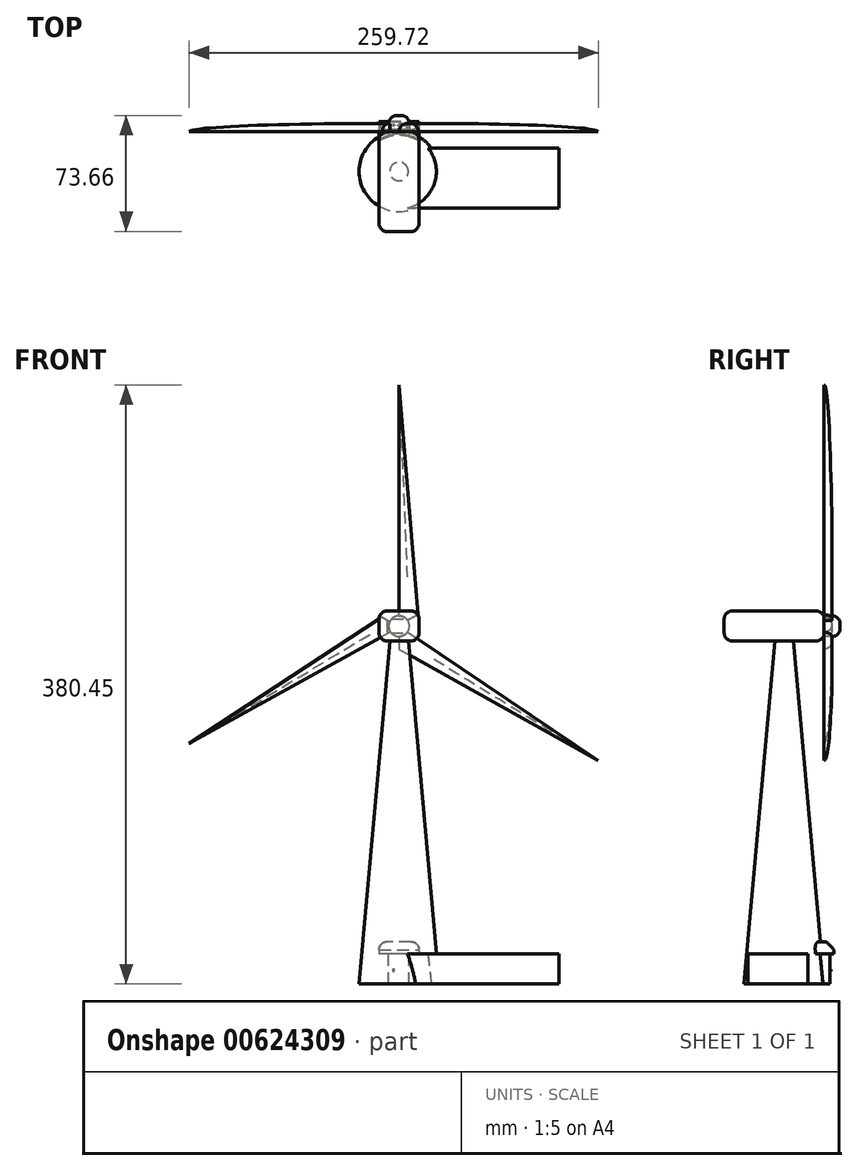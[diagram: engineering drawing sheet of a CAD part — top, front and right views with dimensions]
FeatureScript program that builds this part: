
annotation { "Feature Type Name" : "Feature", "Feature Type Description" : "" }
export const myFeature = defineFeature(function(context is Context, id is Id, definition is map)
    precondition{}
    {
        {
            var Q0;
            Q0=qCreatedBy(makeId("Front.planeOp"),FACE);
            var sketch = newSketch(context, id + "F0", { "sketchPlane" : qUnion([Q0])});
            skLineSegment(sketch, "E0", {"start": v(0, 0) * mm, "end": v(25.4, 0) * mm});
            skLineSegment(sketch, "E1", {"start": v(25.4, 0) * mm, "end": v(5.85, 218.4) * mm});
            skLineSegment(sketch, "E2", {"start": v(5.85, 218.4) * mm, "end": v(0, 217.88) * mm});
            skLineSegment(sketch, "E3", {"start": v(0, 217.88) * mm, "end": v(0, 0) * mm});
            skSolve(sketch);
        }
        {
            var Q0;
            Q0=makeQuery(id+"F0.imprint","IMPRINT",FACE,{"disambiguationData":[TD([[makeQuery(id+"F0.imprint","IMPRINT",EDGE,{"derivedFrom":sQuery(id+"F0.wireOp",EDGE,"E0")}),1.0]])]});
            var Q1;
            Q1=sQuery(id+"F0.wireOp",EDGE,"E3");
            revolve(context, id + "F1", {"entities" : qUnion([Q0]), "axis" : qUnion([Q1]), "revolveType" : RevolveType.FULL});
        }
        {
            var Q0;
            Q0=qCreatedBy(makeId("Top.planeOp"),FACE);
            var Q1;
            Q1 = qBodyType(qCreatedBy(id + "F6bmU4iKGu6LFPM_1" ,EDGE), BodyType.WIRE);
            cPlane(context, id + "F2", {"entities" : qUnion([Q0, Q1]), "cplaneType" : CPlaneType.OFFSET, "offset" : 217.88 * mm, "width" : 152.4 * mm, "height" : 152.4 * mm});
        }
        {
            var Q0;
            Q0=qCreatedBy(id+"F2.planeOp",FACE);
            var sketch = newSketch(context, id + "F3", { "sketchPlane" : qUnion([Q0])});
            skLineSegment(sketch, "E4", {"start": v(0, 0) * mm, "end": v(0, -38.1) * mm});
            skLineSegment(sketch, "E5", {"start": v(0, -38.1) * mm, "end": v(-12.7, -38.1) * mm});
            skLineSegment(sketch, "E6.bottom", {"start": v(-12.7, -38.1) * mm, "end": v(12.7, -38.1) * mm});
            skLineSegment(sketch, "E6.top", {"start": v(-12.7, 25.4) * mm, "end": v(12.7, 25.4) * mm});
            skLineSegment(sketch, "E6.left", {"start": v(-12.7, -38.1) * mm, "end": v(-12.7, 25.4) * mm});
            skLineSegment(sketch, "E6.right", {"start": v(12.7, -38.1) * mm, "end": v(12.7, 25.4) * mm});
            skSolve(sketch);
        }
        {
            var Q0;
            Q0=makeQuery(id+"F3.imprint","IMPRINT",FACE,{"disambiguationData":[TD([[makeQuery(id+"F3.imprint","IMPRINT",EDGE,{"derivedFrom":sQuery(id+"F3.wireOp",EDGE,"E6.top")}),-1.0]])]});
            extrude(context, id + "F4", {"entities" : qUnion([Q0]), "operationType" : NewBodyOperationType.ADD, "depth" : 19.05 * mm, "offsetDistance" : 25.4 * mm});
        }
        {
            var Q0;
            Q0=makeQuery(id+"F4.opExtrude","SWEPT_FACE",FACE,{"disambiguationData":[OSD([sQuery(id+"F3.wireOp",EDGE,"E6.top")])]});
            cPlane(context, id + "F5", {"entities" : qUnion([Q0]), "cplaneType" : CPlaneType.OFFSET, "offset" : 0 * mm, "width" : 152.4 * mm, "height" : 152.4 * mm});
        }
        {
            var Q0;
            Q0=makeQuery(id+"F4.opExtrude","CAP_EDGE",EDGE,{"disambiguationData":[OSD([sQuery(id+"F3.wireOp",EDGE,"E6.left")])],"isStart":false});
            var Q1;
            Q1=makeQuery(id+"F4.opExtrude","CAP_EDGE",EDGE,{"disambiguationData":[OSD([sQuery(id+"F3.wireOp",EDGE,"E6.bottom")])],"isStart":false});
            var Q2;
            Q2=makeQuery(id+"F4.opExtrude","SWEPT_FACE",FACE,{"disambiguationData":[OSD([sQuery(id+"F3.wireOp",EDGE,"E6.bottom")])]});
            var Q3;
            Q3=makeQuery(id+"F4.opExtrude","CAP_EDGE",EDGE,{"disambiguationData":[OSD([sQuery(id+"F3.wireOp",EDGE,"E6.top")])],"isStart":false});
            var Q4;
            Q4=makeQuery(id+"F4.opExtrude","SWEPT_FACE",FACE,{"disambiguationData":[OSD([sQuery(id+"F3.wireOp",EDGE,"E6.top")])]});
            var Q5;
            Q5=makeQuery(id+"F4.opExtrude","CAP_EDGE",EDGE,{"disambiguationData":[OSD([sQuery(id+"F3.wireOp",EDGE,"E6.left")])],"isStart":true});
            var Q6;
            Q6=makeQuery(id+"F4.opExtrude","CAP_EDGE",EDGE,{"disambiguationData":[OSD([sQuery(id+"F3.wireOp",EDGE,"E6.right")])],"isStart":false});
            var Q7;
            Q7=makeQuery(id+"F4.opExtrude","CAP_EDGE",EDGE,{"disambiguationData":[OSD([sQuery(id+"F3.wireOp",EDGE,"E6.right")])],"isStart":true});
            var Q8;
            Q8=makeQuery(id+"F4.opExtrude","SWEPT_FACE",FACE,{"disambiguationData":[OSD([sQuery(id+"F3.wireOp",EDGE,"E6.right")])]});
            fillet(context, id + "F6", {"entities" : qUnion([Q0, Q1, Q2, Q3, Q4, Q5, Q6, Q7, Q8]), "radius" : 5.08 * mm, "tangentPropagation" : true, "allowEdgeOverflow" : false});
        }
        {
            var Q0;
            Q0=qCreatedBy(makeId("Front.planeOp"),FACE);
            var sketch = newSketch(context, id + "F7", { "sketchPlane" : qUnion([Q0])});
            skLineSegment(sketch, "E7.bottom", {"start": v(6.17, 0) * mm, "end": v(-6.53, 0) * mm});
            skLineSegment(sketch, "E7.top", {"start": v(6.17, 19.05) * mm, "end": v(-6.53, 19.05) * mm});
            skLineSegment(sketch, "E7.left", {"start": v(6.17, 0) * mm, "end": v(6.17, 19.05) * mm});
            skLineSegment(sketch, "E7.right", {"start": v(-6.53, 0) * mm, "end": v(-6.53, 19.05) * mm});
            skSolve(sketch);
        }
        {
            var Q0;
            Q0 = qSketchRegion(id + "F7", true);
            extrude(context, id + "F8", {"entities" : qUnion([Q0]), "operationType" : NewBodyOperationType.ADD, "oppositeDirection" : true, "depth" : 29.2 * mm, "offsetDistance" : 25.4 * mm});
        }
        {
            var Q0;
            Q0=qCreatedBy(makeId("Right.planeOp"),FACE);
            var sketch = newSketch(context, id + "F9", { "sketchPlane" : qUnion([Q0])});
            skLineSegment(sketch, "E8.bottom", {"start": v(-23.08, 19.05) * mm, "end": v(15.02, 19.05) * mm});
            skLineSegment(sketch, "E8.top", {"start": v(-23.08, 0) * mm, "end": v(15.02, 0) * mm});
            skLineSegment(sketch, "E8.left", {"start": v(-23.08, 19.05) * mm, "end": v(-23.08, 0) * mm});
            skLineSegment(sketch, "E8.right", {"start": v(15.02, 19.05) * mm, "end": v(15.02, 0) * mm});
            skSolve(sketch);
        }
        {
            var Q0;
            Q0 = qSketchRegion(id + "F9", true);
            extrude(context, id + "F10", {"entities" : qUnion([Q0]), "operationType" : NewBodyOperationType.ADD, "depth" : 101.6 * mm, "offsetDistance" : 25.4 * mm});
        }
        {
            var Q0;
            Q0=qCreatedBy(makeId("Front.planeOp"),FACE);
            var sketch = newSketch(context, id + "F11", { "sketchPlane" : qUnion([Q0])});
            skCircle(sketch, "E9", {"center": v(-3.5, 8.73) * mm, "radius": 0.66 * mm});
            skSolve(sketch);
        }
        {
            var Q0;
            Q0 = qSketchRegion(id + "F11", true);
            extrude(context, id + "F12", {"entities" : qUnion([Q0]), "operationType" : NewBodyOperationType.ADD, "oppositeDirection" : true, "depth" : 29.72 * mm, "offsetDistance" : 25.4 * mm});
        }
        {
            var Q0;
            Q0=qCreatedBy(id+"F5.planeOp",FACE);
            var sketch = newSketch(context, id + "F13", { "sketchPlane" : qUnion([Q0])});
            skCircle(sketch, "E10", {"center": v(0, 227.27) * mm, "radius": 6.55 * mm});
            skSolve(sketch);
        }
        {
            var Q0;
            Q0 = qSketchRegion(id + "F13", true);
            extrude(context, id + "F14", {"entities" : qUnion([Q0]), "operationType" : NewBodyOperationType.ADD, "depth" : 10.16 * mm, "offsetDistance" : 25.4 * mm});
        }
        {
            var Q0;
            Q0=makeQuery(id+"F14.opExtrude","CAP_FACE",FACE,{"disambiguationData":[OSD([sQuery(id+"F13.wireOp",EDGE,"E10")])],"isStart":false});
            fillet(context, id + "F15", {"entities" : qUnion([Q0]), "radius" : 5.08 * mm, "tangentPropagation" : true, "allowEdgeOverflow" : false});
        }
        {
            var Q0;
            Q0=qCreatedBy(id+"F5.planeOp",FACE);
            var sketch = newSketch(context, id + "F16", { "sketchPlane" : qUnion([Q0])});
            skLineSegment(sketch, "E11", {"start": v(0, 227.12) * mm, "end": v(-126.49, 142.1) * mm});
            skLineSegment(sketch, "E12", {"start": v(0, 227.12) * mm, "end": v(0, 212.63) * mm});
            skLineSegment(sketch, "E13", {"start": v(0, 212.63) * mm, "end": v(-126.49, 142.1) * mm});
            skSolve(sketch);
        }
        {
            var Q0;
            Q0=qCreatedBy(id+"F5.planeOp",FACE);
            var sketch = newSketch(context, id + "F17", { "sketchPlane" : qUnion([Q0])});
            skLineSegment(sketch, "E14", {"start": v(0, 226.72) * mm, "end": v(133.23, 152.73) * mm});
            skLineSegment(sketch, "E15", {"start": v(133.23, 152.73) * mm, "end": v(10.85, 233.1) * mm});
            skLineSegment(sketch, "E16", {"start": v(10.85, 233.1) * mm, "end": v(0, 226.72) * mm});
            skSolve(sketch);
        }
        {
            var Q0;
            Q0 = qSketchRegion(id + "F17", true);
            extrude(context, id + "F18", {"entities" : qUnion([Q0]), "operationType" : NewBodyOperationType.ADD, "depth" : 5.08 * mm, "offsetDistance" : 25.4 * mm});
        }
        {
            var Q0;
            Q0=qCreatedBy(id+"F5.planeOp",FACE);
            var sketch = newSketch(context, id + "F19", { "sketchPlane" : qUnion([Q0])});
            skLineSegment(sketch, "E17", {"start": v(0, 228.05) * mm, "end": v(0, 380.45) * mm});
            skLineSegment(sketch, "E18", {"start": v(0, 380.45) * mm, "end": v(-12.18, 234.59) * mm});
            skLineSegment(sketch, "E19", {"start": v(-12.18, 234.59) * mm, "end": v(0, 228.05) * mm});
            skSolve(sketch);
        }
        {
            var Q0;
            Q0=makeQuery(id+"F19.imprint","IMPRINT",FACE,{"disambiguationData":[TD([[makeQuery(id+"F19.imprint","IMPRINT",EDGE,{"derivedFrom":sQuery(id+"F19.wireOp",EDGE,"E17")}),1.0]])]});
            extrude(context, id + "F20", {"entities" : qUnion([Q0]), "operationType" : NewBodyOperationType.ADD, "depth" : 5.08 * mm, "offsetDistance" : 25.4 * mm});
        }
        {
            var Q0;
            Q0 = qSketchRegion(id + "F16", true);
            extrude(context, id + "F21", {"entities" : qUnion([Q0]), "operationType" : NewBodyOperationType.ADD, "depth" : 5.08 * mm, "offsetDistance" : 25.4 * mm});
        }
        {
            var Q0;
            Q0=makeQuery(id+"F20.opExtrude","CAP_EDGE",EDGE,{"disambiguationData":[OSD([sQuery(id+"F19.wireOp",EDGE,"E17")])],"isStart":false});
            var Q1;
            Q1=makeQuery(id+"F20.opExtrude","CAP_EDGE",EDGE,{"disambiguationData":[OSD([sQuery(id+"F19.wireOp",EDGE,"E18")])],"isStart":false});
            var Q2;
            Q2=makeQuery(id+"FDrvfz1r7wtz94q_1.opExtrude","CAP_EDGE",EDGE,{"disambiguationData":[OSD([sQuery(id+"F16.wireOp",EDGE,"E11")])],"isStart":false});
            var Q3;
            Q3=makeQuery(id+"FDrvfz1r7wtz94q_1.opExtrude","CAP_EDGE",EDGE,{"disambiguationData":[OSD([sQuery(id+"F16.wireOp",EDGE,"E13")])],"isStart":false});
            var Q4;
            Q4=makeQuery(id+"F18.opExtrude","CAP_EDGE",EDGE,{"disambiguationData":[OSD([sQuery(id+"F17.wireOp",EDGE,"E14")])],"isStart":false});
            var Q5;
            Q5=makeQuery(id+"F18.opExtrude","CAP_EDGE",EDGE,{"disambiguationData":[OSD([sQuery(id+"F17.wireOp",EDGE,"E15")])],"isStart":false});
            fillet(context, id + "F22", {"entities" : qUnion([Q0, Q1, Q2, Q3, Q4, Q5]), "radius" : 5.08 * mm, "tangentPropagation" : true, "allowEdgeOverflow" : false});
        }
        {
            var Q0;
            Q0=makeQuery(id+"F21.opExtrude","CAP_EDGE",EDGE,{"disambiguationData":[OSD([sQuery(id+"F16.wireOp",EDGE,"E11")])],"isStart":false});
            var Q1;
            Q1=makeQuery(id+"F21.opExtrude","CAP_EDGE",EDGE,{"disambiguationData":[OSD([sQuery(id+"F16.wireOp",EDGE,"E13")])],"isStart":false});
            fillet(context, id + "F23", {"entities" : qUnion([Q0, Q1]), "radius" : 5.08 * mm, "tangentPropagation" : true, "allowEdgeOverflow" : false});
        }
        {
            var Q0;
            Q0=qCreatedBy(makeId("Front.planeOp"),FACE);
            var sketch = newSketch(context, id + "F24", { "sketchPlane" : qUnion([Q0])});
            skLineSegment(sketch, "E20.bottom", {"start": v(12.7, 26.84) * mm, "end": v(-12.7, 26.84) * mm});
            skLineSegment(sketch, "E20.top", {"start": v(12.7, 19.22) * mm, "end": v(-12.7, 19.22) * mm});
            skLineSegment(sketch, "E20.left", {"start": v(12.7, 26.84) * mm, "end": v(12.7, 19.22) * mm});
            skLineSegment(sketch, "E20.right", {"start": v(-12.7, 26.84) * mm, "end": v(-12.7, 19.22) * mm});
            skSolve(sketch);
        }
        {
            var Q0;
            Q0 = qSketchRegion(id + "F24", true);
            extrude(context, id + "F25", {"entities" : qUnion([Q0]), "operationType" : NewBodyOperationType.ADD, "oppositeDirection" : true, "depth" : 31.75 * mm, "offsetDistance" : 25.4 * mm});
        }
        {
            var Q0;
            Q0=makeQuery(id+"F25.opExtrude","CAP_EDGE",EDGE,{"disambiguationData":[OSD([sQuery(id+"F24.wireOp",EDGE,"E20.bottom")])],"isStart":false});
            chamfer(context, id + "F26", {"entities" : qUnion([Q0]), "width" : 5.08 * mm, "tangentPropagation" : true});
        }
        {
            var Q0;
            Q0=makeQuery(id+"F25.opExtrude","SWEPT_EDGE",EDGE,{"disambiguationData":[OSD([sQuery(id+"F24.wireOp",EDGE,"E20.bottom"),sQuery(id+"F24.wireOp",EDGE,"E20.right")])]});
            var Q1;
            Q1=makeQuery(id+"F25.opExtrude","SWEPT_EDGE",EDGE,{"disambiguationData":[OSD([sQuery(id+"F24.wireOp",EDGE,"E20.bottom"),sQuery(id+"F24.wireOp",EDGE,"E20.left")])]});
            fillet(context, id + "F27", {"entities" : qUnion([Q0, Q1]), "radius" : 5.08 * mm, "tangentPropagation" : true, "allowEdgeOverflow" : false});
        }
    });
